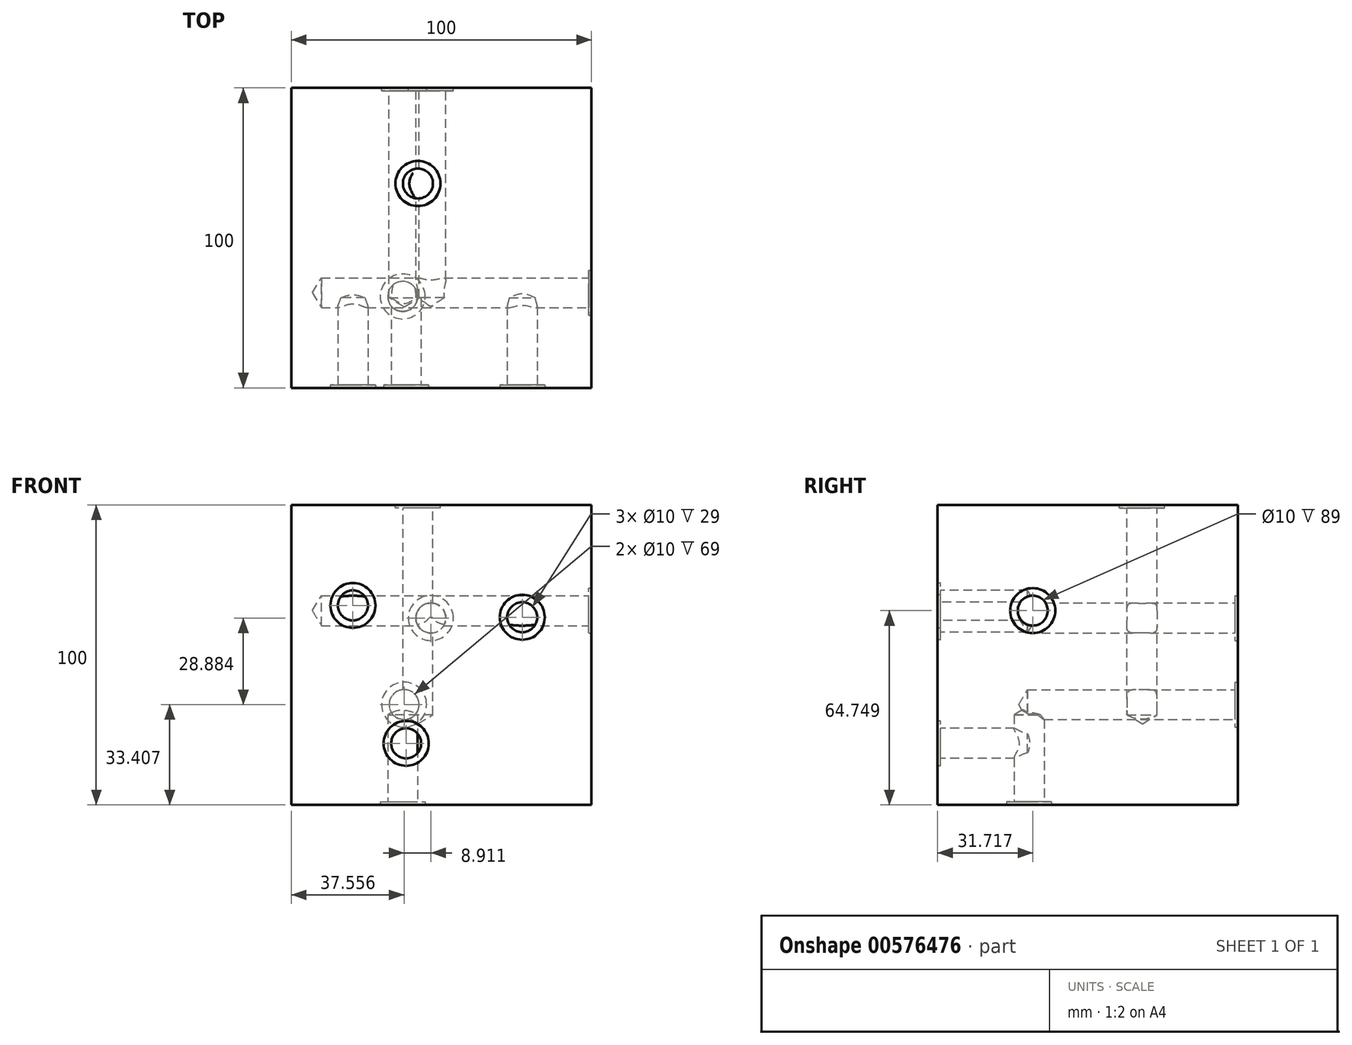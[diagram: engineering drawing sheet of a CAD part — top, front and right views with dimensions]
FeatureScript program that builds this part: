
annotation { "Feature Type Name" : "Feature", "Feature Type Description" : "" }
export const myFeature = defineFeature(function(context is Context, id is Id, definition is map)
    precondition{}
    {
        {
            var Q0;
            Q0=qCreatedBy(makeId("Front.planeOp"),FACE);
            var sketch = newSketch(context, id + "F0", { "sketchPlane" : qUnion([Q0])});
            skLineSegment(sketch, "E0.bottom", {"start": v(50, 50) * mm, "end": v(-50, 50) * mm});
            skLineSegment(sketch, "E0.top", {"start": v(50, -50) * mm, "end": v(-50, -50) * mm});
            skLineSegment(sketch, "E0.left", {"start": v(50, 50) * mm, "end": v(50, -50) * mm});
            skLineSegment(sketch, "E0.right", {"start": v(-50, 50) * mm, "end": v(-50, -50) * mm});
            skPoint(sketch, "E0.middle", {"position": v(0, 0) * mm});
            skSolve(sketch);
        }
        {
            var Q0;
            Q0=makeQuery(id+"F0.imprint","IMPRINT",FACE,{"disambiguationData":[TD([[makeQuery(id+"F0.imprint","IMPRINT",EDGE,{"derivedFrom":sQuery(id+"F0.wireOp",EDGE,"E0.bottom")}),1.0]])]});
            extrude(context, id + "F1", {"entities" : qUnion([Q0]), "endBound" : BoundingType.SYMMETRIC, "depth" : 100 * mm, "offsetDistance" : 25 * mm});
        }
        {
            var Q0;
            Q0=makeQuery(id+"F1.opExtrude","CAP_FACE",FACE,{"disambiguationData":[OSD([sQuery(id+"F0.wireOp",EDGE,"E0.bottom"),sQuery(id+"F0.wireOp",EDGE,"E0.top"),sQuery(id+"F0.wireOp",EDGE,"E0.left"),sQuery(id+"F0.wireOp",EDGE,"E0.right")])],"isStart":false});
            var sketch = newSketch(context, id + "F2", { "sketchPlane" : qUnion([Q0])});
            skPoint(sketch, "E1", {"position": v(-29.5, 16.48) * mm});
            skPoint(sketch, "E2", {"position": v(26.92, 12.55) * mm});
            skPoint(sketch, "E3", {"position": v(-11.76, -29.49) * mm});
            skSolve(sketch);
        }
        {
            var Q0;
            Q0=sQuery(id+"F2.wireOp",VERTEX,"E1");
            var Q1;
            Q1=sQuery(id+"F2.wireOp",VERTEX,"E2");
            var Q2;
            Q2=sQuery(id+"F2.wireOp",VERTEX,"E3");
            var Q3;
            Q3=makeQuery(id+"F1.opExtrude","SWEPT_BODY",BODY,{"disambiguationData":[OSD([sQuery(id+"F0.wireOp",EDGE,"E0.bottom"),sQuery(id+"F0.wireOp",EDGE,"E0.top"),sQuery(id+"F0.wireOp",EDGE,"E0.left"),sQuery(id+"F0.wireOp",EDGE,"E0.right")])]});
            hole(context, id + "F3", {"style" : HoleStyle.C_BORE, "endStyle" : HoleEndStyle.BLIND, "holeDiameter" : 10 * mm, "cBoreDiameter" : 15 * mm, "cBoreDepth" : 1 * mm, "holeDepth" : 30 * mm, "tappedDepth" : 12 * mm, "tapClearance" : 3, "startFromSketch" : true, "locations" : qUnion([Q0, Q1, Q2]), "scope" : qUnion([Q3])});
        }
        {
            var Q0;
            Q0=makeQuery(id+"F1.opExtrude","SWEPT_FACE",FACE,{"disambiguationData":[OSD([sQuery(id+"F0.wireOp",EDGE,"E0.left")])]});
            var sketch = newSketch(context, id + "F4", { "sketchPlane" : qUnion([Q0])});
            skPoint(sketch, "E4", {"position": v(-18.28, 14.75) * mm});
            skSolve(sketch);
        }
        {
            var Q0;
            Q0=sQuery(id+"F4.wireOp",VERTEX,"E4");
            var Q1;
            Q1=makeQuery(id+"F1.opExtrude","SWEPT_BODY",BODY,{"disambiguationData":[OSD([sQuery(id+"F0.wireOp",EDGE,"E0.bottom"),sQuery(id+"F0.wireOp",EDGE,"E0.top"),sQuery(id+"F0.wireOp",EDGE,"E0.left"),sQuery(id+"F0.wireOp",EDGE,"E0.right")])]});
            hole(context, id + "F5", {"style" : HoleStyle.C_BORE, "endStyle" : HoleEndStyle.BLIND, "holeDiameter" : 10 * mm, "cBoreDiameter" : 15 * mm, "cBoreDepth" : 1 * mm, "holeDepth" : 90 * mm, "tappedDepth" : 12 * mm, "tapClearance" : 3, "startFromSketch" : true, "locations" : qUnion([Q0]), "scope" : qUnion([Q1])});
        }
        {
            var Q0;
            Q0=makeQuery(id+"F1.opExtrude","SWEPT_FACE",FACE,{"disambiguationData":[OSD([sQuery(id+"F0.wireOp",EDGE,"E0.top")])]});
            var sketch = newSketch(context, id + "F6", { "sketchPlane" : qUnion([Q0])});
            skPoint(sketch, "E5", {"position": v(-12.9, 19.51) * mm});
            skSolve(sketch);
        }
        {
            var Q0;
            Q0=sQuery(id+"F6.wireOp",VERTEX,"E5");
            var Q1;
            Q1=makeQuery(id+"F1.opExtrude","SWEPT_BODY",BODY,{"disambiguationData":[OSD([sQuery(id+"F0.wireOp",EDGE,"E0.bottom"),sQuery(id+"F0.wireOp",EDGE,"E0.top"),sQuery(id+"F0.wireOp",EDGE,"E0.left"),sQuery(id+"F0.wireOp",EDGE,"E0.right")])]});
            hole(context, id + "F7", {"style" : HoleStyle.C_BORE, "endStyle" : HoleEndStyle.BLIND, "holeDiameter" : 10 * mm, "cBoreDiameter" : 15 * mm, "cBoreDepth" : 1 * mm, "holeDepth" : 30 * mm, "tappedDepth" : 12 * mm, "tapClearance" : 3, "startFromSketch" : true, "locations" : qUnion([Q0]), "scope" : qUnion([Q1])});
        }
        {
            var Q0;
            Q0=makeQuery(id+"F1.opExtrude","CAP_FACE",FACE,{"disambiguationData":[OSD([sQuery(id+"F0.wireOp",EDGE,"E0.bottom"),sQuery(id+"F0.wireOp",EDGE,"E0.top"),sQuery(id+"F0.wireOp",EDGE,"E0.left"),sQuery(id+"F0.wireOp",EDGE,"E0.right")])],"isStart":true});
            var sketch = newSketch(context, id + "F8", { "sketchPlane" : qUnion([Q0])});
            skPoint(sketch, "E6", {"position": v(12.44, -16.6) * mm});
            skPoint(sketch, "E7", {"position": v(3.53, 12.3) * mm});
            skSolve(sketch);
        }
        {
            var Q0;
            Q0=sQuery(id+"F8.wireOp",VERTEX,"E7");
            var Q1;
            Q1=sQuery(id+"F8.wireOp",VERTEX,"E6");
            var Q2;
            Q2=makeQuery(id+"F1.opExtrude","SWEPT_BODY",BODY,{"disambiguationData":[OSD([sQuery(id+"F0.wireOp",EDGE,"E0.bottom"),sQuery(id+"F0.wireOp",EDGE,"E0.top"),sQuery(id+"F0.wireOp",EDGE,"E0.left"),sQuery(id+"F0.wireOp",EDGE,"E0.right")])]});
            hole(context, id + "F9", {"style" : HoleStyle.C_BORE, "endStyle" : HoleEndStyle.BLIND, "holeDiameter" : 10 * mm, "cBoreDiameter" : 15 * mm, "cBoreDepth" : 1 * mm, "holeDepth" : 70 * mm, "tappedDepth" : 12 * mm, "tapClearance" : 3, "startFromSketch" : true, "locations" : qUnion([Q0, Q1]), "scope" : qUnion([Q2])});
        }
        {
            var Q0;
            Q0=makeQuery(id+"F1.opExtrude","SWEPT_FACE",FACE,{"disambiguationData":[OSD([sQuery(id+"F0.wireOp",EDGE,"E0.bottom")])]});
            var sketch = newSketch(context, id + "F10", { "sketchPlane" : qUnion([Q0])});
            skPoint(sketch, "E8", {"position": v(-7.84, 18.13) * mm});
            skSolve(sketch);
        }
        {
            var Q0;
            Q0=sQuery(id+"F10.wireOp",VERTEX,"E8");
            var Q1;
            Q1=makeQuery(id+"F1.opExtrude","SWEPT_BODY",BODY,{"disambiguationData":[OSD([sQuery(id+"F0.wireOp",EDGE,"E0.bottom"),sQuery(id+"F0.wireOp",EDGE,"E0.top"),sQuery(id+"F0.wireOp",EDGE,"E0.left"),sQuery(id+"F0.wireOp",EDGE,"E0.right")])]});
            hole(context, id + "F11", {"style" : HoleStyle.C_BORE, "endStyle" : HoleEndStyle.BLIND, "holeDiameter" : 10 * mm, "cBoreDiameter" : 15 * mm, "cBoreDepth" : 1 * mm, "holeDepth" : 70 * mm, "tappedDepth" : 12 * mm, "tapClearance" : 3, "startFromSketch" : true, "locations" : qUnion([Q0]), "scope" : qUnion([Q1])});
        }
    });
